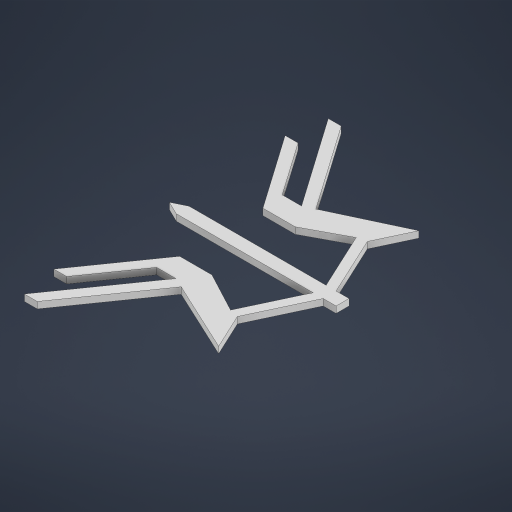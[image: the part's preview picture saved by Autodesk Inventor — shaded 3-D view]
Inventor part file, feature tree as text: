
AUTODESK INVENTOR PART (.ipt)
format: ipt  version: 2024.3 (Build 283343000, 343)  size: 226,816 bytes
history: native  units: mm
features: extrude x1, sketch x1
ambient origin geometry x8: Origin, YZ Plane, XZ Plane, XY Plane, X Axis, Y Axis, Z Axis, Center Point
bodies: Solid1 (feature_tree)
feature tree (2):
  extrude  "Extrusion1"  Depth=10.0mm
  sketch  "Sketch1"  dims[d2=5.0mm d4=10.0mm d6=5.0mm d7=90.0deg d8=10.0mm d9=90.0deg d10=50.0mm d12=30.0mm d13=22.68928mm d14=60.0mm d15=80.0mm d16=17.453293mm d17=10.0mm d18=21.816616mm d19=15.0mm d20=9.599311mm d21=50.0mm d22=21.816616mm d23=10.0mm d24=21.816616mm d25=70.0mm d26=9.599311mm d27=5.0mm d28=0.0mm]
